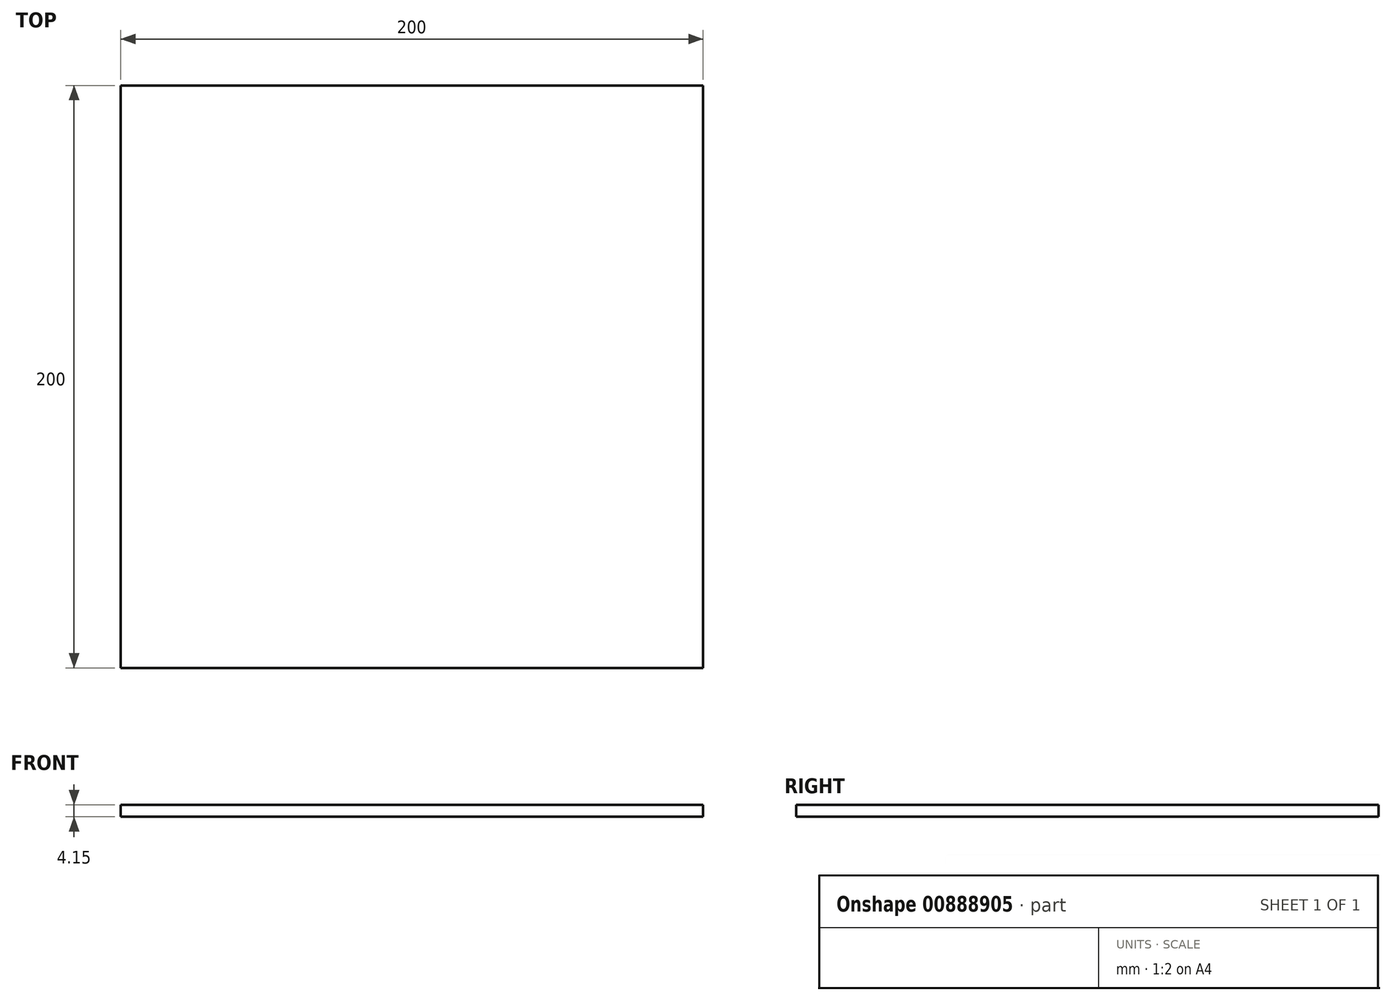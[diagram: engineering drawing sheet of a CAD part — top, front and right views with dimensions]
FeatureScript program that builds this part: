
annotation { "Feature Type Name" : "Feature", "Feature Type Description" : "" }
export const myFeature = defineFeature(function(context is Context, id is Id, definition is map)
    precondition{}
    {
        {
            var Q0;
            Q0=qCreatedBy(makeId("Top.planeOp"),FACE);
            var sketch = newSketch(context, id + "F0", { "sketchPlane" : qUnion([Q0])});
            skLineSegment(sketch, "E0.bottom", {"start": v(-100, -100) * mm, "end": v(100, -100) * mm});
            skLineSegment(sketch, "E0.top", {"start": v(-100, 100) * mm, "end": v(100, 100) * mm});
            skLineSegment(sketch, "E0.left", {"start": v(-100, -100) * mm, "end": v(-100, 100) * mm});
            skLineSegment(sketch, "E0.right", {"start": v(100, -100) * mm, "end": v(100, 100) * mm});
            skLineSegment(sketch, "E1", {"start": v(-100, 0) * mm, "end": v(100, 0) * mm, "construction": true});
            skSolve(sketch);
        }
        {
            var Q0;
            Q0 = qSketchRegion(id + "F0", true);
            extrude(context, id + "F1", {"entities" : qUnion([Q0]), "depth" : 4.15 * mm, "offsetDistance" : 25 * mm});
        }
    });
